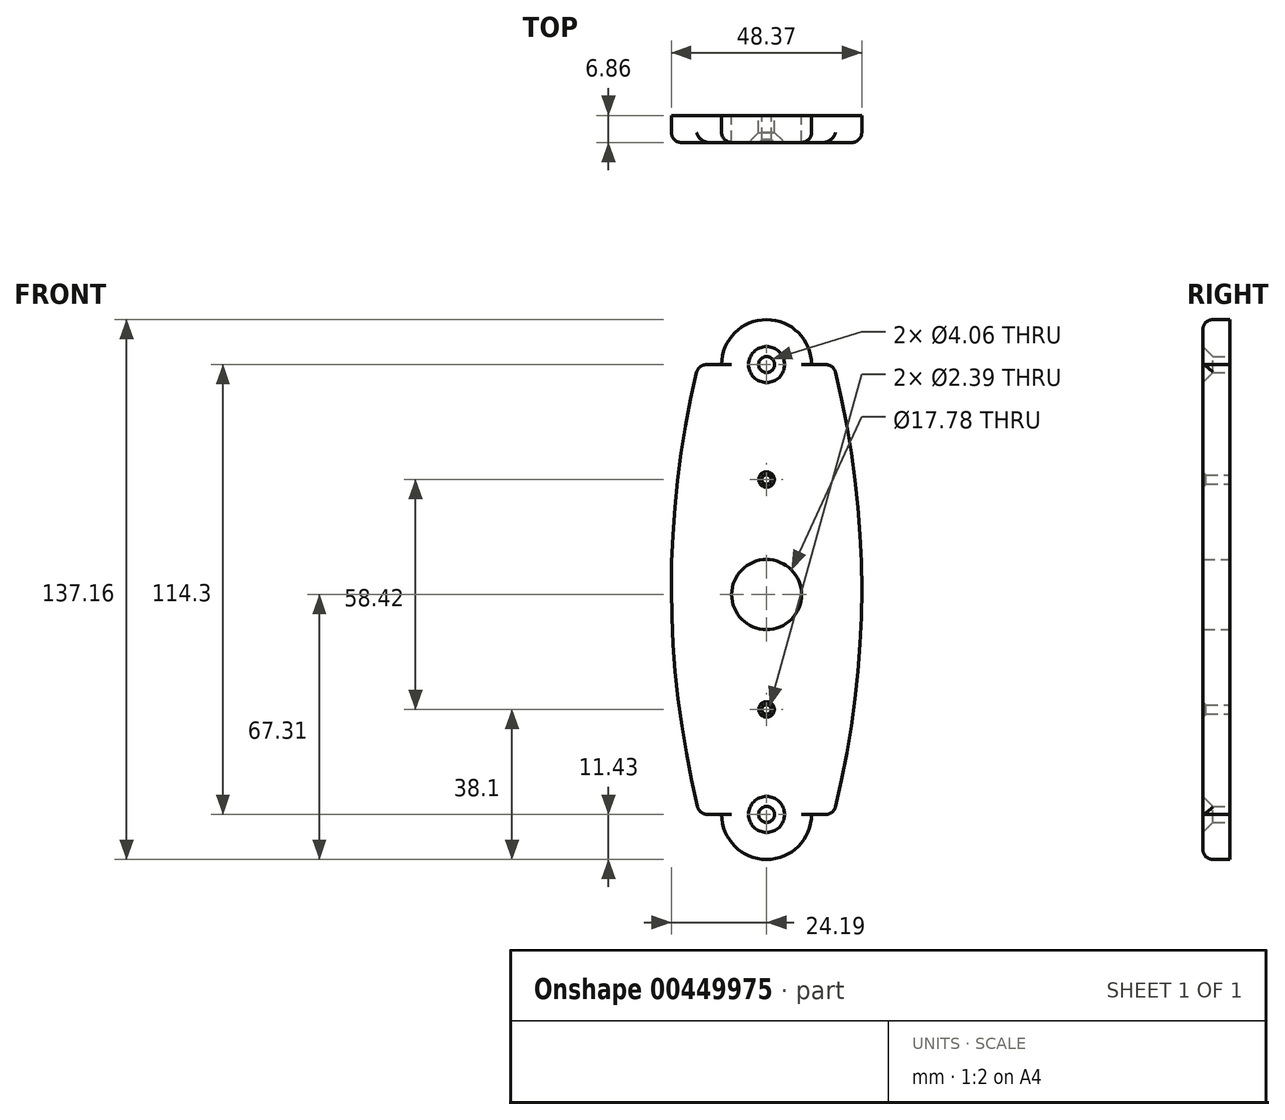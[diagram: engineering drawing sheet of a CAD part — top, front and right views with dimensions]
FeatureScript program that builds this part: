
annotation { "Feature Type Name" : "Feature", "Feature Type Description" : "" }
export const myFeature = defineFeature(function(context is Context, id is Id, definition is map)
    precondition{}
    {
        {
            var Q0;
            Q0=qCreatedBy(makeId("Front.planeOp"),FACE);
            var sketch = newSketch(context, id + "F0", { "sketchPlane" : qUnion([Q0])});
            skCircle(sketch, "E0", {"center": v(0, 0) * mm, "radius": 8.9 * mm});
            skCircle(sketch, "E1", {"center": v(0, 29.21) * mm, "radius": 1.2 * mm});
            skCircle(sketch, "E2", {"center": v(0, 58.42) * mm, "radius": 2.03 * mm});
            skCircle(sketch, "E3", {"center": v(0, -29.21) * mm, "radius": 1.2 * mm});
            skCircle(sketch, "E4", {"center": v(0, -55.88) * mm, "radius": 2.03 * mm});
            skArc(sketch, "E5", {"start": v(-11.43, 58.42) * mm, "mid": v(0, 69.85) * mm, "end": v(11.43, 58.42) * mm});
            skArc(sketch, "E6", {"start": v(11.43, -55.88) * mm, "mid": v(0, -67.31) * mm, "end": v(-11.43, -55.88) * mm});
            skLineSegment(sketch, "E7", {"start": v(0, 69.85) * mm, "end": v(0, -67.31) * mm});
            skLineSegment(sketch, "E8", {"start": v(11.43, 58.42) * mm, "end": v(17.02, 58.42) * mm});
            skLineSegment(sketch, "E9", {"start": v(-11.43, 58.42) * mm, "end": v(-17.28, 58.42) * mm});
            skLineSegment(sketch, "E10", {"start": v(11.43, -55.88) * mm, "end": v(17.02, -55.88) * mm});
            skLineSegment(sketch, "E11", {"start": v(-11.43, -55.88) * mm, "end": v(-17.02, -55.88) * mm});
            skLineSegment(sketch, "E12", {"start": v(0, 0) * mm, "end": v(24.18, 0) * mm});
            skLineSegment(sketch, "E13", {"start": v(0, 0) * mm, "end": v(-24.18, 0) * mm});
            skArc(sketch, "E14", {"start": v(-17.28, 58.42) * mm, "mid": v(-24.19, 1.25) * mm, "end": v(-17.02, -55.88) * mm});
            skArc(sketch, "E15", {"start": v(17.02, -55.88) * mm, "mid": v(24.18, 1.27) * mm, "end": v(17.02, 58.42) * mm});
            skSolve(sketch);
        }
        {
            var Q0;
            Q0 = qSketchRegion(id + "F0", true);
            extrude(context, id + "F1", {"entities" : qUnion([Q0]), "depth" : 6.86 * mm});
        }
        {
            var Q0;
            Q0=makeQuery(id+"F1.opExtrude","CAP_EDGE",EDGE,{"disambiguationData":[OSD([sQuery(id+"F0.wireOp",EDGE,"E5")])],"isStart":false});
            var Q1;
            Q1=makeQuery(id+"F1.opExtrude","CAP_EDGE",EDGE,{"disambiguationData":[OSD([sQuery(id+"F0.wireOp",EDGE,"E15")])],"isStart":false});
            var Q2;
            Q2=makeQuery(id+"F1.opExtrude","CAP_EDGE",EDGE,{"disambiguationData":[OSD([sQuery(id+"F0.wireOp",EDGE,"E14")])],"isStart":false});
            var Q3;
            Q3=makeQuery(id+"F1.opExtrude","CAP_EDGE",EDGE,{"disambiguationData":[OSD([sQuery(id+"F0.wireOp",EDGE,"E6")])],"isStart":false});
            var Q4;
            Q4=makeQuery(id+"F1.opExtrude","SWEPT_EDGE",EDGE,{"disambiguationData":[OSD([sQuery(id+"F0.wireOp",EDGE,"E8"),sQuery(id+"F0.wireOp",EDGE,"E15")])]});
            var Q5;
            Q5=makeQuery(id+"F1.opExtrude","SWEPT_EDGE",EDGE,{"disambiguationData":[OSD([sQuery(id+"F0.wireOp",EDGE,"E9"),sQuery(id+"F0.wireOp",EDGE,"E14")])]});
            var Q6;
            Q6=makeQuery(id+"F1.opExtrude","SWEPT_EDGE",EDGE,{"disambiguationData":[OSD([sQuery(id+"F0.wireOp",EDGE,"E11"),sQuery(id+"F0.wireOp",EDGE,"E14")])]});
            var Q7;
            Q7=makeQuery(id+"F1.opExtrude","SWEPT_EDGE",EDGE,{"disambiguationData":[OSD([sQuery(id+"F0.wireOp",EDGE,"E10"),sQuery(id+"F0.wireOp",EDGE,"E15")])]});
            fillet(context, id + "F2", {"entities" : qUnion([Q0, Q1, Q2, Q3, Q4, Q5, Q6, Q7]), "radius" : 2.54 * mm, "tangentPropagation" : true, "allowEdgeOverflow" : false});
        }
        {
            var Q0;
            Q0=makeQuery(id+"F1.opExtrude","CAP_EDGE",EDGE,{"disambiguationData":[OSD([sQuery(id+"F0.wireOp",EDGE,"E4")])],"isStart":false});
            var Q1;
            Q1=makeQuery(id+"F1.opExtrude","CAP_EDGE",EDGE,{"disambiguationData":[OSD([sQuery(id+"F0.wireOp",EDGE,"E2")])],"isStart":false});
            chamfer(context, id + "F3", {"entities" : qUnion([Q0, Q1]), "width" : 2.54 * mm, "tangentPropagation" : true});
        }
        {
            var Q0;
            Q0=makeQuery(id+"F1.opExtrude","CAP_EDGE",EDGE,{"disambiguationData":[OSD([sQuery(id+"F0.wireOp",EDGE,"E1")])],"isStart":false});
            var Q1;
            Q1=makeQuery(id+"F1.opExtrude","CAP_EDGE",EDGE,{"disambiguationData":[OSD([sQuery(id+"F0.wireOp",EDGE,"E3")])],"isStart":false});
            chamfer(context, id + "F4", {"entities" : qUnion([Q0, Q1]), "width" : 0.76 * mm, "tangentPropagation" : true});
        }
    });
